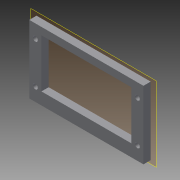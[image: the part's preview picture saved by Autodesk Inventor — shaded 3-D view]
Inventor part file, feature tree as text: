
AUTODESK INVENTOR PART (.ipt)
format: ipt  version: 2015 (Build 190159000, 159)  size: 112,128 bytes
history: native  units: in
note: dims shown in document units (in); Inventor stores cm internally (conversion verified against a paired STEP export)
features: extrude x3, sketch x3, plane x1, reference x1
ambient origin geometry x8: Origin, YZ Plane, XZ Plane, XY Plane, X Axis, Y Axis, Z Axis, Center Point
bodies: Solid1 (feature_tree)
feature tree (8):
  plane  "Work Plane1"
  extrude  "Extrusion1"  Depth=0.1969in
  extrude  "Extrusion2"  Depth=0.1181in TaperAngle=0.0deg
  extrude  "Extrusion3"  Depth=0.1181in
  sketch  "Sketch1"  dims[d0=0.1181in d1=0.0in d2=0.1969in]
  reference  "Reference1"
  sketch  "Sketch2"  dims[d3=0.1969in d4=0.1181in d5=0.0in]
  sketch  "Sketch4"  dims[d6=0.0984in d7=0.0984in d8=0.0984in d9=0.0984in d10=0.1181in d11=0.0in]
